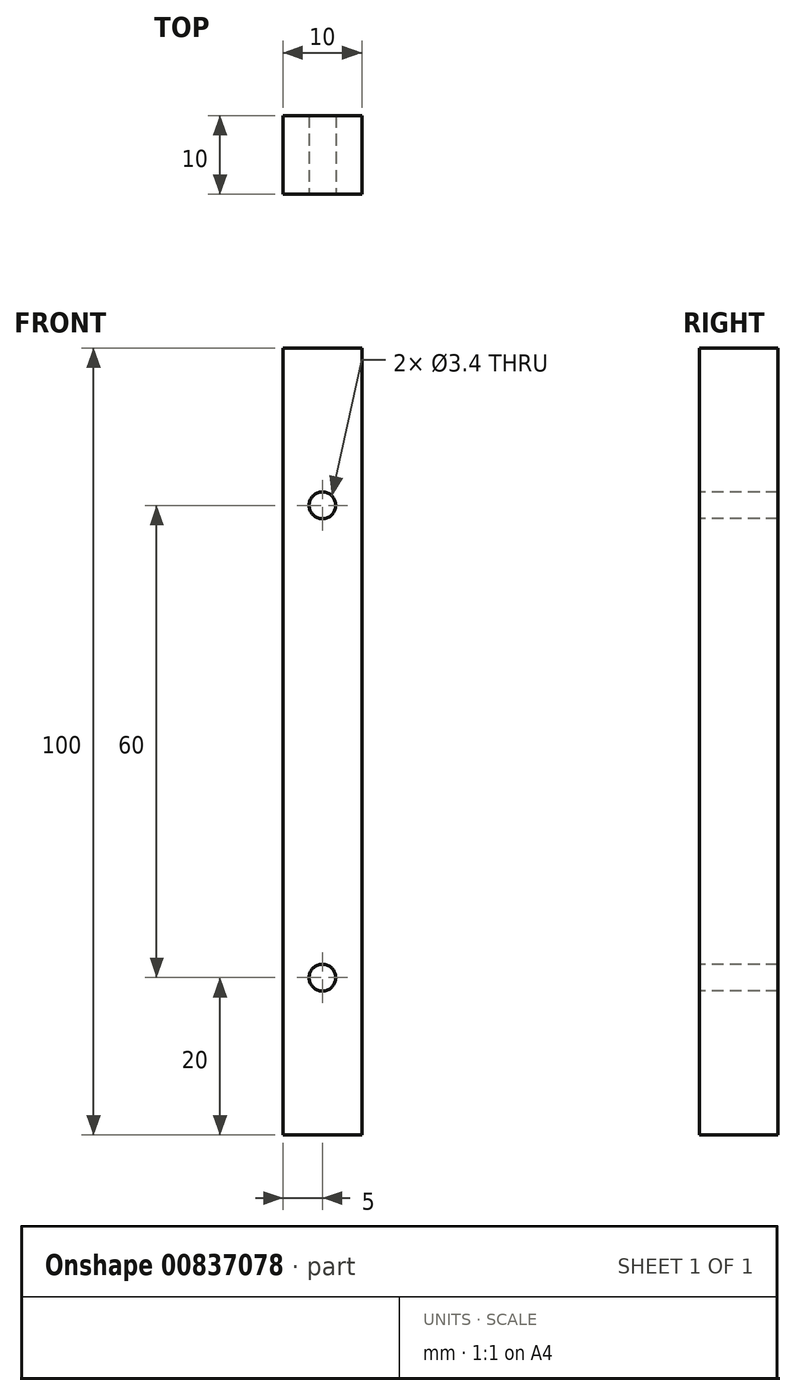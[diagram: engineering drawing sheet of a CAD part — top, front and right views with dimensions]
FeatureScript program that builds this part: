
annotation { "Feature Type Name" : "Feature", "Feature Type Description" : "" }
export const myFeature = defineFeature(function(context is Context, id is Id, definition is map)
    precondition{}
    {
        {
            var Q0;
            Q0=qCreatedBy(makeId("Top.planeOp"),FACE);
            var sketch = newSketch(context, id + "F0", { "sketchPlane" : qUnion([Q0])});
            skLineSegment(sketch, "E0.bottom", {"start": v(-5, 5) * mm, "end": v(5, 5) * mm});
            skLineSegment(sketch, "E0.top", {"start": v(-5, -5) * mm, "end": v(5, -5) * mm});
            skLineSegment(sketch, "E0.left", {"start": v(-5, 5) * mm, "end": v(-5, -5) * mm});
            skLineSegment(sketch, "E0.right", {"start": v(5, 5) * mm, "end": v(5, -5) * mm});
            skPoint(sketch, "E0.middle", {"position": v(0, 0) * mm});
            skSolve(sketch);
        }
        {
            var Q0;
            Q0=makeQuery(id+"F0.imprint","IMPRINT",FACE,{"disambiguationData":[TD([[makeQuery(id+"F0.imprint","IMPRINT",EDGE,{"derivedFrom":sQuery(id+"F0.wireOp",EDGE,"E0.bottom")}),-1.0]])]});
            extrude(context, id + "F1", {"entities" : qUnion([Q0]), "depth" : 100 * mm, "offsetDistance" : 25 * mm});
        }
        {
            var Q0;
            Q0=makeQuery(id+"F1.opExtrude","SWEPT_FACE",FACE,{"disambiguationData":[OSD([sQuery(id+"F0.wireOp",EDGE,"E0.top")])]});
            var sketch = newSketch(context, id + "F2", { "sketchPlane" : qUnion([Q0])});
            skLineSegment(sketch, "E1", {"start": v(0, 0) * mm, "end": v(-44.51, 0) * mm, "construction": true});
            skLineSegment(sketch, "E2", {"start": v(-52.46, 20) * mm, "end": v(26.05, 20) * mm, "construction": true});
            skLineSegment(sketch, "E3", {"start": v(-48.67, 80) * mm, "end": v(29.91, 80) * mm, "construction": true});
            skLineSegment(sketch, "E4", {"start": v(0, 0) * mm, "end": v(0, 114.1) * mm, "construction": true});
            skPoint(sketch, "E5", {"position": v(0, 80) * mm});
            skPoint(sketch, "E6", {"position": v(0, 20) * mm});
            skSolve(sketch);
        }
        {
            var Q0;
            Q0=sQuery(id+"F2.wireOp",VERTEX,"E5");
            var Q1;
            Q1=sQuery(id+"F2.wireOp",VERTEX,"E6");
            var Q2;
            Q2=makeQuery(id+"F1.opExtrude","SWEPT_BODY",BODY,{"disambiguationData":[OSD([sQuery(id+"F0.wireOp",EDGE,"E0.bottom"),sQuery(id+"F0.wireOp",EDGE,"E0.top"),sQuery(id+"F0.wireOp",EDGE,"E0.left"),sQuery(id+"F0.wireOp",EDGE,"E0.right")])]});
            hole(context, id + "F3", {"style" : HoleStyle.SIMPLE, "endStyle" : HoleEndStyle.THROUGH, "standardTappedOrClearance" : lookupTablePath({ "fit" : "Normal", "standard" : "ISO", "size" : "M3", "type" : "Clearance" }), "standardBlindInLast" : lookupTablePath({ "fit" : "Normal", "standard" : "ISO", "engagement" : "75%", "pitch" : "0.5 mm", "size" : "M3", "type" : "Clearance & tapped" }), "holeDiameter" : 3.4 * mm, "majorDiameter" : 5 * mm, "isTappedThrough" : true, "tappedDepth" : 12 * mm, "tapClearance" : 3, "startFromSketch" : true, "locations" : qUnion([Q0, Q1]), "scope" : qUnion([Q2])});
        }
    });
